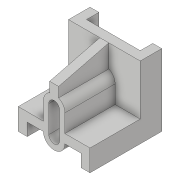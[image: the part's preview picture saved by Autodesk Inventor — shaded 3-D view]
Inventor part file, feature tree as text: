
AUTODESK INVENTOR PART (.ipt)
format: ipt  version: 2017 (Build 210142000, 142)  size: 143,360 bytes
history: native  units: in
note: dims shown in document units (in); Inventor stores cm internally (conversion verified against a paired STEP export)
features: sketch x4, extrude x3, shell x1, plane x1, rib x1, projected_geometry x1
ambient origin geometry x8: Origin, YZ Plane, XZ Plane, XY Plane, X Axis, Y Axis, Z Axis, Center Point
bodies: Solid1 (feature_tree)
feature tree (11):
  extrude  "Extrusion1"  Depth=1.575in
  shell  "Shell1"  Thickness=0.472in
  extrude  "Extrusion2"  Depth=0.197in
  extrude  "Extrusion3"  Depth=0.236in
  plane  "Work Plane1"
  rib  "Rib1"
  sketch  "Sketch1"  dims[d0=1.575in d1=1.575in d2=0.472in]
  sketch  "Sketch2"  dims[d3=1.575in d4=0.0in d5=0.197in]
  sketch  "Sketch3"  dims[d6=0.236in d7=0.59in]
  sketch  "Sketch4"  dims[d8=0.787in d9=1.575in d10=0.0in d12=0.118in d13=1.575in d14=0.0in d15=0.197in d16=0.1in d17=0.197in d18=0.0in d19=0.0in d20=0.1in d21=0.1in]
  projected_geometry  "Project Cut Edges1"
